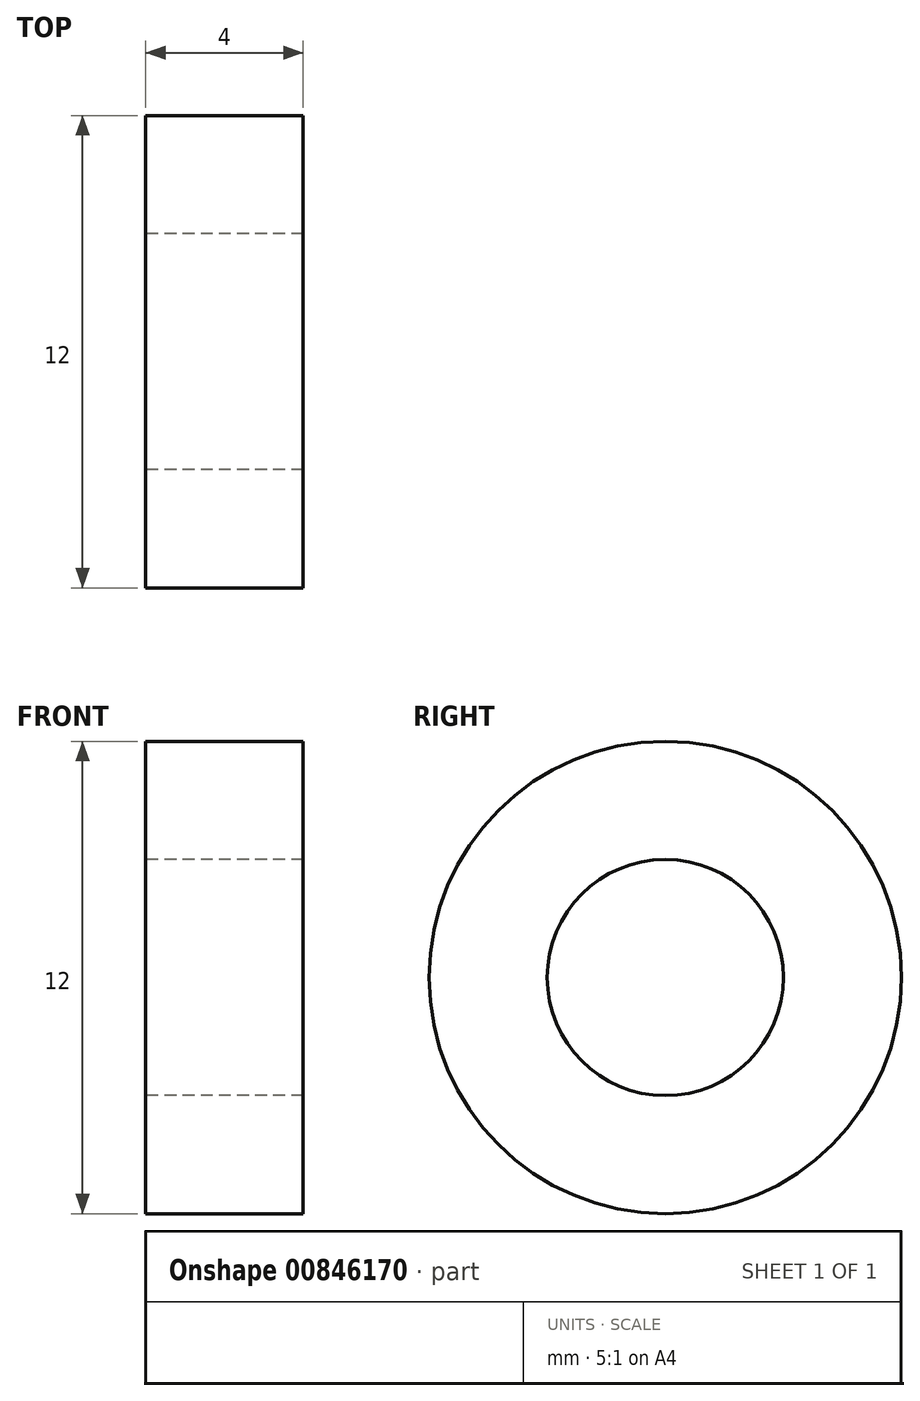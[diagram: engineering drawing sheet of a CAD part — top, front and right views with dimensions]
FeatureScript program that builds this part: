
annotation { "Feature Type Name" : "Feature", "Feature Type Description" : "" }
export const myFeature = defineFeature(function(context is Context, id is Id, definition is map)
    precondition{}
    {
        {
            var Q0;
            Q0=qCreatedBy(makeId("Right.planeOp"),FACE);
            var sketch = newSketch(context, id + "F0", { "sketchPlane" : qUnion([Q0])});
            skCircle(sketch, "E0", {"center": v(0, 0) * mm, "radius": 3 * mm});
            skCircle(sketch, "E1", {"center": v(0, 0) * mm, "radius": 6 * mm});
            skSolve(sketch);
        }
        {
            var Q0;
            Q0=makeQuery(id+"F0.imprint","IMPRINT",FACE,{"disambiguationData":[TD([[makeQuery(id+"F0.imprint","IMPRINT",EDGE,{"derivedFrom":sQuery(id+"F0.wireOp",EDGE,"E0")}),-1.0]])]});
            extrude(context, id + "F1", {"entities" : qUnion([Q0]), "depth" : 4 * mm, "offsetDistance" : 25 * mm});
        }
    });
